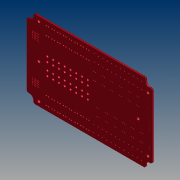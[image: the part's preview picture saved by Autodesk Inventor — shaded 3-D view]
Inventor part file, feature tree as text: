
AUTODESK INVENTOR PART (.ipt)
format: ipt  version: 2012 (Build 160160000, 160)  size: 1,178,624 bytes
history: native  units: mm (DEFAULTED — no unit token found)
features: imported_body x1, extrude x1, sketch x1, projected_geometry x1
ambient origin geometry x8: Origin, YZ Plane, XZ Plane, XY Plane, X Axis, Y Axis, Z Axis, Center Point
bodies: Solid1 (feature_tree)
feature tree (4):
  imported_body  "Base1"
  extrude  "Extrusion1"  [1 undecoded]
  sketch  "Sketch1"  dims[d0=2.3876mm d1=0.0mm]
  projected_geometry  "Projected Loop1"
note: 1 required parameter value undecoded (feature->parameter linkage not recoverable at this tier; creation-order binding heuristic only, values carry confidence <= 0.55)
